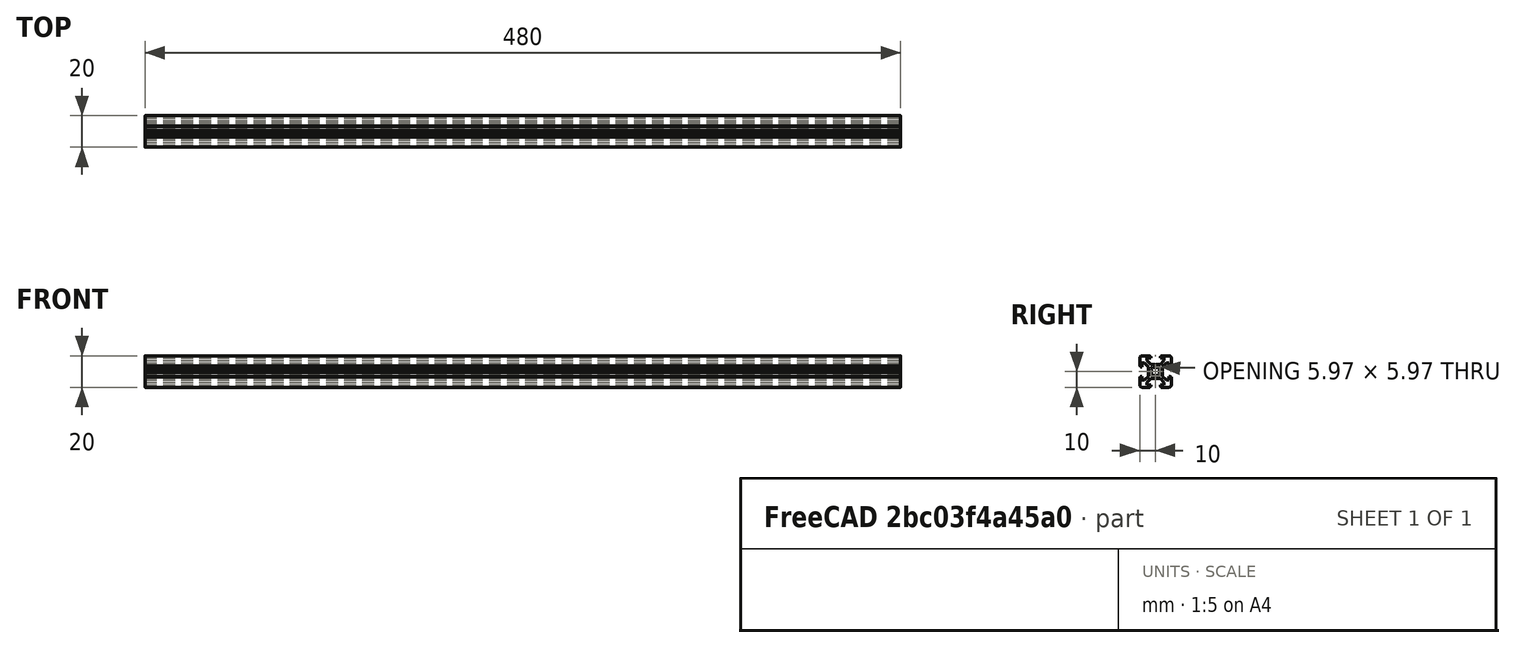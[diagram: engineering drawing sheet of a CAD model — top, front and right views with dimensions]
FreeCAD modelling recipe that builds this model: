
FCSTD DOCUMENT  (FreeCAD 0.19R)
Label: T-Slot-Profil
License: All rights reserved
LicenseURL: http://en.wikipedia.org/wiki/All_rights_reserved
objects: Sketcher::SketchObject×1, PartDesign::Pad×1, PartDesign::Body×1
note: 4 computed .brp shape members not serialized (recipe doc carries the construction recipe); baked Part::Feature solids carry a one-line shape summary decoded from their .brp

FEATURE [Sketcher::SketchObject] Sketch  label="T-Slot-Skizze"
  FullyConstrained = true
  MapMode = 5
  Placement = pos=(0,0,0) rot=(0.57735,0.57735,0.57735;2.0944rad)
  Support = -> [YZ_Plane]
  sketch-geometry (98):
    g0: LineSegment StartX=0 StartY=4.1 StartZ=0 EndX=0.65 EndY=4.5 EndZ=0
    g1: LineSegment StartX=0.65 StartY=4.5 StartZ=0 EndX=3 EndY=4.5 EndZ=0
    g2: LineSegment StartX=3 StartY=4.5 StartZ=0 EndX=5.5 EndY=7 EndZ=0
    g3: LineSegment StartX=5.5 StartY=7 StartZ=0 EndX=5.5 EndY=8.5 EndZ=0
    g4: LineSegment StartX=5.5 StartY=8.5 StartZ=0 EndX=3 EndY=8.5 EndZ=0
    g5: LineSegment StartX=3 StartY=8.5 StartZ=0 EndX=3 EndY=9.5 EndZ=0
    g6: LineSegment StartX=3 StartY=9.5 StartZ=0 EndX=3.5 EndY=9.5 EndZ=0
    g7: LineSegment StartX=3.5 StartY=9.5 StartZ=0 EndX=3.5 EndY=10 EndZ=0
    g8: LineSegment StartX=3.5 StartY=10 StartZ=0 EndX=8.5 EndY=10 EndZ=0
    g9: LineSegment StartX=10 StartY=8.5 StartZ=0 EndX=10 EndY=3.5 EndZ=0
    g10: LineSegment StartX=10 StartY=3.5 StartZ=0 EndX=9.5 EndY=3.5 EndZ=0
    g11: LineSegment StartX=9.5 StartY=3.5 StartZ=0 EndX=9.5 EndY=3 EndZ=0
    g12: LineSegment StartX=9.5 StartY=3 StartZ=0 EndX=8.5 EndY=3 EndZ=0
    g13: LineSegment StartX=8.5 StartY=3 StartZ=0 EndX=8.5 EndY=5.5 EndZ=0
    g14: LineSegment StartX=8.5 StartY=5.5 StartZ=0 EndX=7 EndY=5.5 EndZ=0
    g15: LineSegment StartX=7 StartY=5.5 StartZ=0 EndX=4.5 EndY=3 EndZ=0
    g16: LineSegment StartX=4.5 StartY=3 StartZ=0 EndX=4.5 EndY=0.65 EndZ=0
    g17: LineSegment StartX=4.5 StartY=0.65 StartZ=0 EndX=4.1 EndY=0 EndZ=0
    g18: ArcOfCircle CenterX=8.5 CenterY=8.5 CenterZ=0 NormalX=0 NormalY=0 NormalZ=1 AngleXU=0 Radius=1.5 StartAngle=0 EndAngle=1.5708
    g19: LineSegment StartX=0 StartY=-4.1 StartZ=0 EndX=0.65 EndY=-4.5 EndZ=0
    g20: LineSegment StartX=0.65 StartY=-4.5 StartZ=0 EndX=3 EndY=-4.5 EndZ=0
    g21: LineSegment StartX=3 StartY=-4.5 StartZ=0 EndX=5.5 EndY=-7 EndZ=0
    g22: LineSegment StartX=5.5 StartY=-7 StartZ=0 EndX=5.5 EndY=-8.5 EndZ=0
    g23: LineSegment StartX=5.5 StartY=-8.5 StartZ=0 EndX=3 EndY=-8.5 EndZ=0
    g24: LineSegment StartX=3 StartY=-8.5 StartZ=0 EndX=3 EndY=-9.5 EndZ=0
    g25: LineSegment StartX=3 StartY=-9.5 StartZ=0 EndX=3.5 EndY=-9.5 EndZ=0
    g26: LineSegment StartX=3.5 StartY=-9.5 StartZ=0 EndX=3.5 EndY=-10 EndZ=0
    g27: LineSegment StartX=3.5 StartY=-10 StartZ=0 EndX=8.5 EndY=-10 EndZ=0
    g28: LineSegment StartX=10 StartY=-8.5 StartZ=0 EndX=10 EndY=-3.5 EndZ=0
    g29: LineSegment StartX=10 StartY=-3.5 StartZ=0 EndX=9.5 EndY=-3.5 EndZ=0
    g30: LineSegment StartX=9.5 StartY=-3.5 StartZ=0 EndX=9.5 EndY=-3 EndZ=0
    g31: LineSegment StartX=9.5 StartY=-3 StartZ=0 EndX=8.5 EndY=-3 EndZ=0
    g32: LineSegment StartX=8.5 StartY=-3 StartZ=0 EndX=8.5 EndY=-5.5 EndZ=0
    g33: LineSegment StartX=8.5 StartY=-5.5 StartZ=0 EndX=7 EndY=-5.5 EndZ=0
    g34: LineSegment StartX=7 StartY=-5.5 StartZ=0 EndX=4.5 EndY=-3 EndZ=0
    g35: LineSegment StartX=4.5 StartY=-3 StartZ=0 EndX=4.5 EndY=-0.65 EndZ=0
    g36: ArcOfCircle CenterX=8.5 CenterY=-8.5 CenterZ=0 NormalX=0 NormalY=0 NormalZ=1 AngleXU=0 Radius=1.5 StartAngle=4.71239 EndAngle=6.28319
    g37: LineSegment StartX=4.5 StartY=-0.65 StartZ=0 EndX=4.1 EndY=0 EndZ=0
    g38: LineSegment StartX=0 StartY=-4.1 StartZ=0 EndX=-0.65 EndY=-4.5 EndZ=0
    g39: LineSegment StartX=-0.65 StartY=-4.5 StartZ=0 EndX=-3 EndY=-4.5 EndZ=0
    g40: LineSegment StartX=-3 StartY=-4.5 StartZ=0 EndX=-5.5 EndY=-7 EndZ=0
    g41: LineSegment StartX=-5.5 StartY=-7 StartZ=0 EndX=-5.5 EndY=-8.5 EndZ=0
    g42: LineSegment StartX=-5.5 StartY=-8.5 StartZ=0 EndX=-3 EndY=-8.5 EndZ=0
    g43: LineSegment StartX=-3 StartY=-8.5 StartZ=0 EndX=-3 EndY=-9.5 EndZ=0
    g44: LineSegment StartX=-3 StartY=-9.5 StartZ=0 EndX=-3.5 EndY=-9.5 EndZ=0
    g45: LineSegment StartX=-3.5 StartY=-9.5 StartZ=0 EndX=-3.5 EndY=-10 EndZ=0
    g46: LineSegment StartX=-3.5 StartY=-10 StartZ=0 EndX=-8.5 EndY=-10 EndZ=0
    g47: LineSegment StartX=-10 StartY=-8.5 StartZ=0 EndX=-10 EndY=-3.5 EndZ=0
    g48: LineSegment StartX=-10 StartY=-3.5 StartZ=0 EndX=-9.5 EndY=-3.5 EndZ=0
    g49: LineSegment StartX=-9.5 StartY=-3.5 StartZ=0 EndX=-9.5 EndY=-3 EndZ=0
    g50: LineSegment StartX=-9.5 StartY=-3 StartZ=0 EndX=-8.5 EndY=-3 EndZ=0
    g51: LineSegment StartX=-8.5 StartY=-3 StartZ=0 EndX=-8.5 EndY=-5.5 EndZ=0
    g52: LineSegment StartX=-8.5 StartY=-5.5 StartZ=0 EndX=-7 EndY=-5.5 EndZ=0
    g53: LineSegment StartX=-7 StartY=-5.5 StartZ=0 EndX=-4.5 EndY=-3 EndZ=0
    g54: LineSegment StartX=-4.5 StartY=-3 StartZ=0 EndX=-4.5 EndY=-0.65 EndZ=0
    g55: ArcOfCircle CenterX=-8.5 CenterY=-8.5 CenterZ=0 NormalX=0 NormalY=0 NormalZ=1 AngleXU=0 Radius=1.5 StartAngle=3.14159 EndAngle=4.71239
    g56: LineSegment StartX=-4.5 StartY=-0.65 StartZ=0 EndX=-4.1 EndY=0 EndZ=0
    g57: LineSegment StartX=-0.65 StartY=4.5 StartZ=0 EndX=-3 EndY=4.5 EndZ=0
    g58: LineSegment StartX=-3 StartY=4.5 StartZ=0 EndX=-5.5 EndY=7 EndZ=0
    g59: LineSegment StartX=-5.5 StartY=7 StartZ=0 EndX=-5.5 EndY=8.5 EndZ=0
    g60: LineSegment StartX=-5.5 StartY=8.5 StartZ=0 EndX=-3 EndY=8.5 EndZ=0
    g61: LineSegment StartX=-3 StartY=8.5 StartZ=0 EndX=-3 EndY=9.5 EndZ=0
    g62: LineSegment StartX=-3 StartY=9.5 StartZ=0 EndX=-3.5 EndY=9.5 EndZ=0
    g63: LineSegment StartX=-3.5 StartY=9.5 StartZ=0 EndX=-3.5 EndY=10 EndZ=0
    g64: LineSegment StartX=-3.5 StartY=10 StartZ=0 EndX=-8.5 EndY=10 EndZ=0
    g65: LineSegment StartX=-10 StartY=8.5 StartZ=0 EndX=-10 EndY=3.5 EndZ=0
    g66: LineSegment StartX=-10 StartY=3.5 StartZ=0 EndX=-9.5 EndY=3.5 EndZ=0
    g67: LineSegment StartX=-9.5 StartY=3.5 StartZ=0 EndX=-9.5 EndY=3 EndZ=0
    g68: LineSegment StartX=-9.5 StartY=3 StartZ=0 EndX=-8.5 EndY=3 EndZ=0
    g69: LineSegment StartX=-8.5 StartY=3 StartZ=0 EndX=-8.5 EndY=5.5 EndZ=0
    g70: LineSegment StartX=-8.5 StartY=5.5 StartZ=0 EndX=-7 EndY=5.5 EndZ=0
    g71: LineSegment StartX=-7 StartY=5.5 StartZ=0 EndX=-4.5 EndY=3 EndZ=0
    g72: LineSegment StartX=-4.5 StartY=3 StartZ=0 EndX=-4.5 EndY=0.65 EndZ=0
    g73: ArcOfCircle CenterX=-8.5 CenterY=8.5 CenterZ=0 NormalX=0 NormalY=0 NormalZ=1 AngleXU=0 Radius=1.5 StartAngle=1.5708 EndAngle=3.14159
    g74: LineSegment StartX=-4.5 StartY=0.65 StartZ=0 EndX=-4.1 EndY=0 EndZ=0
    g75: LineSegment StartX=0 StartY=4.1 StartZ=0 EndX=-0.65 EndY=4.5 EndZ=0
    g76: Circle CenterX=0 CenterY=0 CenterZ=0 NormalX=0 NormalY=0 NormalZ=1 AngleXU=0 Radius=3.55
    g77: Circle CenterX=0 CenterY=0 CenterZ=0 NormalX=0 NormalY=0 NormalZ=1 AngleXU=0 Radius=2.75
    g78: LineSegment StartX=1.3405 StartY=2.40116 StartZ=0 EndX=1.92324 EndY=2.9839 EndZ=0
    g79: LineSegment StartX=1.92324 StartY=2.9839 StartZ=0 EndX=2.9839 EndY=1.92324 EndZ=0
    g80: LineSegment StartX=2.9839 StartY=1.92324 StartZ=0 EndX=2.40116 EndY=1.3405 EndZ=0
    g81: ArcOfCircle CenterX=0 CenterY=0 CenterZ=0 NormalX=0 NormalY=0 NormalZ=1 AngleXU=0 Radius=2.75 StartAngle=0 EndAngle=0.509172
    g82: ArcOfCircle CenterX=0 CenterY=0 CenterZ=0 NormalX=0 NormalY=0 NormalZ=1 AngleXU=0 Radius=2.75 StartAngle=1.06162 EndAngle=1.5708
    g83: LineSegment StartX=-1.3405 StartY=2.40116 StartZ=0 EndX=-1.92324 EndY=2.9839 EndZ=0
    g84: LineSegment StartX=-1.92324 StartY=2.9839 StartZ=0 EndX=-2.9839 EndY=1.92324 EndZ=0
    g85: LineSegment StartX=-2.9839 StartY=1.92324 StartZ=0 EndX=-2.40116 EndY=1.3405 EndZ=0
    g86: ArcOfCircle CenterX=-1.3e-15 CenterY=6e-16 CenterZ=0 NormalX=0 NormalY=0 NormalZ=1 AngleXU=0 Radius=2.75 StartAngle=2.63242 EndAngle=3.14159
    g87: ArcOfCircle CenterX=-1.3e-15 CenterY=6e-16 CenterZ=0 NormalX=0 NormalY=0 NormalZ=1 AngleXU=0 Radius=2.75 StartAngle=1.5708 EndAngle=2.07997
    g88: LineSegment StartX=-1.34051 StartY=-2.40115 StartZ=0 EndX=-1.92325 EndY=-2.98389 EndZ=0
    g89: LineSegment StartX=-1.92325 StartY=-2.98389 StartZ=0 EndX=-2.9839 EndY=-1.92323 EndZ=0
    g90: LineSegment StartX=-2.9839 StartY=-1.92323 StartZ=0 EndX=-2.40116 EndY=-1.34049 EndZ=0
    g91: ArcOfCircle CenterX=-3e-16 CenterY=2e-16 CenterZ=0 NormalX=0 NormalY=0 NormalZ=1 AngleXU=0 Radius=2.75 StartAngle=3.14159 EndAngle=3.65076
    g92: ArcOfCircle CenterX=-3e-16 CenterY=2e-16 CenterZ=0 NormalX=0 NormalY=0 NormalZ=1 AngleXU=0 Radius=2.75 StartAngle=4.20321 EndAngle=4.71239
    g93: LineSegment StartX=1.34051 StartY=-2.40115 StartZ=0 EndX=1.92325 EndY=-2.98389 EndZ=0
    g94: LineSegment StartX=1.92325 StartY=-2.98389 StartZ=0 EndX=2.9839 EndY=-1.92323 EndZ=0
    g95: LineSegment StartX=2.9839 StartY=-1.92323 StartZ=0 EndX=2.40116 EndY=-1.34049 EndZ=0
    g96: ArcOfCircle CenterX=3e-16 CenterY=2e-16 CenterZ=0 NormalX=0 NormalY=0 NormalZ=1 AngleXU=0 Radius=2.75 StartAngle=4.71239 EndAngle=5.22156
    g97: ArcOfCircle CenterX=3e-16 CenterY=2e-16 CenterZ=0 NormalX=0 NormalY=0 NormalZ=1 AngleXU=0 Radius=2.75 StartAngle=5.77402 EndAngle=6.28319
  constraints (291):
    c: PointOnObject(g0,g-2)
    c: Coincident(g0,g1)
    c: Horizontal(g1)
    c: Coincident(g1,g2)
    c: Coincident(g2,g3)
    c: Vertical(g3)
    c: Coincident(g3,g4)
    c: Horizontal(g4)
    c: Coincident(g4,g5)
    c: Vertical(g5)
    c: Coincident(g5,g6)
    c: Horizontal(g6)
    c: Coincident(g6,g7)
    c: Coincident(g7,g8)
    c: Horizontal(g8)
    c: Vertical(g7)
    c: DistanceX(g-1,g5) = 3
    c: DistanceY(g4,g7) = 1.5
    c: DistanceY(g0,g7) = 5.5
    c: DistanceY(g3,g3) = 1.5
    c: DistanceY(g4,g5) = 1
    c: DistanceX(g-1,g1) = 3
    c: DistanceX(g-1,g7) = 3.5
    c: DistanceX(g0,g0) = 0.65
    c: DistanceY(g0,g0) = 0.4
    c: DistanceX(g-1,g3) = 5.5
    c: Vertical(g9)
    c: Coincident(g9,g10)
    c: Coincident(g10,g11)
    c: Coincident(g11,g12)
    c: Coincident(g12,g13)
    c: Vertical(g13)
    c: Coincident(g13,g14)
    c: Horizontal(g14)
    c: Coincident(g14,g15)
    c: Coincident(g15,g16)
    c: Vertical(g16)
    c: Coincident(g16,g17)
    c: PointOnObject(g17,g-1)
    c: Horizontal(g10)
    c: Horizontal(g12)
    c: Vertical(g11)
    c: Equal(g17,g0)
    c: Equal(g1,g16)
    c: Equal(g15,g2)
    c: Equal(g3,g14)
    c: Equal(g13,g4)
    c: Equal(g12,g5)
    c: Parallel(g15,g2)
    c: Equal(g11,g6)
    c: Equal(g10,g7)
    c: Equal(g9,g8)
    c: Tangent(g8,g18) = 1.5708
    c: Tangent(g9,g18) = 1.5708
    c: Radius(g18) = 1.5
    c: DistanceY(g-1,g8) = 10
    c: DistanceX(g-1,g9) = 10
    c: Coincident(g19,g20)
    c: Horizontal(g20)
    c: Coincident(g20,g21)
    c: Coincident(g21,g22)
    c: Vertical(g22)
    c: Coincident(g22,g23)
    c: Horizontal(g23)
    c: Coincident(g23,g24)
    c: Vertical(g24)
    c: Coincident(g24,g25)
    c: Horizontal(g25)
    c: Coincident(g25,g26)
    c: Coincident(g26,g27)
    c: Horizontal(g27)
    c: Vertical(g26)
    c: Vertical(g28)
    c: Coincident(g28,g29)
    c: Coincident(g29,g30)
    c: Coincident(g30,g31)
    c: Coincident(g31,g32)
    c: Vertical(g32)
    c: Coincident(g32,g33)
    c: Horizontal(g33)
    c: Coincident(g33,g34)
    c: Coincident(g34,g35)
    c: Vertical(g35)
    c: Coincident(g35,g37)
    c: Horizontal(g29)
    c: Horizontal(g31)
    c: Vertical(g30)
    c: Equal(g37,g19)
    c: Equal(g20,g35)
    c: Equal(g34,g21)
    c: Equal(g22,g33)
    c: Equal(g32,g23)
    c: Equal(g31,g24)
    c: Parallel(g34,g21)
    c: Equal(g30,g25)
    c: Equal(g29,g26)
    c: Equal(g28,g27)
    c: Tangent(g27,g36) = -1.5708
    c: Tangent(g28,g36) = -1.5708
    c: Radius(g36) = 1.5
    c: Equal(g9,g28)
    c: Equal(g12,g31)
    c: DistanceX(g-1,g28) = 10
    c: DistanceY(g27,g-1) = 10
    c: DistanceY(g30,g-1) = 3
    c: Equal(g33,g14)
    c: Equal(g35,g16)
    c: Equal(g17,g37)
    c: Coincident(g37,g17)
    c: Equal(g15,g34)
    c: PointOnObject(g19,g-2)
    c: DistanceY(g34,g-1) = 3
    c: DistanceX(g-1,g20) = 3
    c: Coincident(g38,g39)
    c: Horizontal(g39)
    c: Coincident(g39,g40)
    c: Coincident(g40,g41)
    c: Vertical(g41)
    c: Coincident(g41,g42)
    c: Horizontal(g42)
    c: Coincident(g42,g43)
    c: Vertical(g43)
    c: Coincident(g43,g44)
    c: Horizontal(g44)
    c: Coincident(g44,g45)
    c: Coincident(g45,g46)
    c: Horizontal(g46)
    c: Vertical(g45)
    c: Vertical(g47)
    c: Coincident(g47,g48)
    c: Coincident(g48,g49)
    c: Coincident(g49,g50)
    c: Coincident(g50,g51)
    c: Vertical(g51)
    c: Coincident(g51,g52)
    c: Horizontal(g52)
    c: Coincident(g52,g53)
    c: Coincident(g53,g54)
    c: Vertical(g54)
    c: Coincident(g54,g56)
    c: Horizontal(g48)
    c: Horizontal(g50)
    c: Vertical(g49)
    c: Equal(g39,g54)
    c: Equal(g53,g40)
    c: Equal(g41,g52)
    c: Equal(g51,g42)
    c: Equal(g50,g43)
    c: Parallel(g53,g40)
    c: Equal(g49,g44)
    c: Equal(g48,g45)
    c: Equal(g47,g46)
    c: Tangent(g46,g55) = 1.5708
    c: Tangent(g47,g55) = 1.5708
    c: Radius(g55) = 1.5
    c: Coincident(g38,g19)
    c: DistanceX(g39,g-1) = 3
    c: DistanceX(g38,g19) = 0.65
    c: DistanceY(g38,g19) = 0.4
    c: PointOnObject(g56,g-1)
    c: Equal(g56,g38)
    c: DistanceY(g53,g-1) = 3
    c: Equal(g22,g41)
    c: Equal(g42,g23)
    c: Equal(g24,g43)
    c: Equal(g25,g44)
    c: Equal(g26,g45)
    c: DistanceY(g46,g-1) = 10
    c: DistanceX(g47,g-1) = 10
    c: Coincident(g75,g57)
    c: Horizontal(g57)
    c: Coincident(g57,g58)
    c: Coincident(g58,g59)
    c: Vertical(g59)
    c: Coincident(g59,g60)
    c: Horizontal(g60)
    c: Coincident(g60,g61)
    c: Vertical(g61)
    c: Coincident(g61,g62)
    c: Horizontal(g62)
    c: Coincident(g62,g63)
    c: Coincident(g63,g64)
    c: Horizontal(g64)
    c: Vertical(g63)
    c: Vertical(g65)
    c: Coincident(g65,g66)
    c: Coincident(g66,g67)
    c: Coincident(g67,g68)
    c: Coincident(g68,g69)
    c: Vertical(g69)
    c: Coincident(g69,g70)
    c: Horizontal(g70)
    c: Coincident(g70,g71)
    c: Coincident(g71,g72)
    c: Vertical(g72)
    c: Coincident(g72,g74)
    c: Horizontal(g66)
    c: Horizontal(g68)
    c: Vertical(g67)
    c: Equal(g57,g72)
    c: Equal(g71,g58)
    c: Equal(g59,g70)
    c: Equal(g69,g60)
    c: Equal(g68,g61)
    c: Parallel(g71,g58)
    c: Equal(g67,g62)
    c: Equal(g66,g63)
    c: Equal(g65,g64)
    c: Tangent(g64,g73) = -1.5708
    c: Tangent(g65,g73) = -1.5708
    c: Radius(g73) = 1.5
    c: Equal(g74,g75)
    c: Coincident(g56,g74)
    c: Coincident(g0,g75)
    c: Equal(g0,g75)
    c: Equal(g1,g57)
    c: Equal(g2,g58)
    c: Equal(g3,g59)
    c: Equal(g4,g60)
    c: Equal(g5,g61)
    c: Equal(g6,g62)
    c: Equal(g7,g63)
    c: Equal(g8,g64)
    c: DistanceX(g65,g-1) = 10
    c: Coincident(g76,g-1)
    c: Coincident(g77,g-1)
    c: Radius(g76) = 3.55
    c: Radius(g77) = 2.75
    c: PointOnObject(g78,g77)
    c: PointOnObject(g78,g76)
    c: Coincident(g78,g79)
    c: PointOnObject(g79,g76)
    c: Coincident(g79,g80)
    c: PointOnObject(g80,g77)
    c: Coincident(g81,g-1)
    c: Coincident(g81,g80)
    c: Coincident(g82,g81)
    c: Coincident(g82,g78)
    c: Parallel(g78,g80)
    c: Parallel(g78,g2)
    c: Distance(g79) = 1.5
    c: Distance(g78,g80) = 1.5
    c: PointOnObject(g82,g-2)
    c: PointOnObject(g81,g-1)
    c: Coincident(g83,g84)
    c: Coincident(g84,g85)
    c: Coincident(g86,g85)
    c: Coincident(g87,g86)
    c: Coincident(g87,g83)
    c: Parallel(g83,g85)
    c: Distance(g84) = 1.5
    c: Distance(g83,g85) = 1.5
    c: Coincident(g82,g87)
    c: PointOnObject(g86,g-1)
    c: PointOnObject(g83,g76)
    c: PointOnObject(g83,g77)
    c: PointOnObject(g85,g77)
    c: PointOnObject(g84,g76)
    c: PointOnObject(g86,g77)
    c: Parallel(g85,g71)
    c: Coincident(g88,g89)
    c: Coincident(g89,g90)
    c: Coincident(g91,g90)
    c: Coincident(g92,g91)
    c: Coincident(g92,g88)
    c: Parallel(g88,g90)
    c: Distance(g89) = 1.5
    c: Distance(g88,g90) = 1.5
    c: PointOnObject(g88,g77)
    c: PointOnObject(g90,g77)
    c: Coincident(g86,g91)
    c: PointOnObject(g89,g76)
    c: PointOnObject(g88,g76)
    c: PointOnObject(g92,g-2)
    c: PointOnObject(g92,g77)
    c: Parallel(g88,g40)
    c: Coincident(g93,g94)
    c: Coincident(g94,g95)
    c: Coincident(g97,g95)
    c: Coincident(g96,g97)
    c: Coincident(g96,g93)
    c: Parallel(g93,g95)
    c: Distance(g94) = 1.5
    c: Distance(g93,g95) = 1.5
    c: Coincident(g81,g97)
    c: Coincident(g92,g96)
    c: PointOnObject(g93,g77)
    c: PointOnObject(g95,g77)
    c: PointOnObject(g94,g76)
    c: PointOnObject(g93,g76)
    c: Parallel(g93,g21)
FEATURE [PartDesign::Pad] Pad
  Direction = (1,1,1)
  Length = 480
  Length2 = 100
  Placement = pos=(0,0,0) rot=(0.57735,0.57735,0.57735;2.0944rad)
  Profile = -> Sketch
  Type = 0
FEATURE [PartDesign::Body] Body  label="T-Slot-Profil 20x20"
  Group = -> [Sketch,Pad]
  Origin = -> Origin
  Tip = -> Pad
